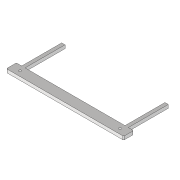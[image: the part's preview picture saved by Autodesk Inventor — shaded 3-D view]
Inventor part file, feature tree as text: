
AUTODESK INVENTOR PART (.ipt)
format: ipt  version: 2020 (Build 240168000, 168)  size: 120,832 bytes
history: native  units: mm
features: extrude x3, sketch x3, chamfer x1
ambient origin geometry x8: Origin, YZ Plane, XZ Plane, XY Plane, X Axis, Y Axis, Z Axis, Center Point
bodies: Volumenkörper1 (feature_tree)
feature tree (7):
  extrude  "Extrusion1"  Depth=600.0mm
  extrude  "Extrusion2"  Depth=1500.0mm
  extrude  "Extrusion3"  Depth=50.0mm TaperAngle=0.0deg
  chamfer  "Fase1"  Distance=85.0mm
  sketch  "Skizze1"  dims[d0=50.0mm d1=600.0mm]
  sketch  "Skizze2"  dims[d2=150.0mm d3=1500.0mm]
  sketch  "Skizze3"  dims[d4=80.0mm d5=50.0mm d6=0.0mm d7=85.0mm d8=85.0mm d9=1500.0mm d10=75.0mm d11=25.0mm d12=0.0mm d13=35.0mm d14=35.0mm d15=0.0mm d16=0.0mm d17=10.0mm d18=2.0mm d19=45.0deg]
